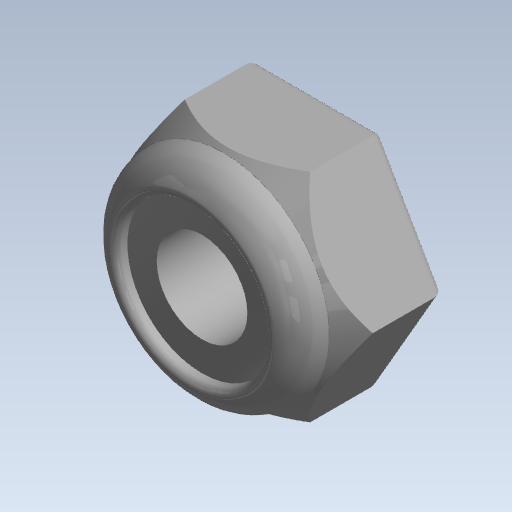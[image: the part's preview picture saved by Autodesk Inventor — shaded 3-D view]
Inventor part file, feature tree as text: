
AUTODESK INVENTOR PART (.ipt)
format: ipt  version: 2020 (Build 240168000, 168)  size: 135,680 bytes
history: native  units: mm (DEFAULTED — no unit token found)
features: fillet x1
ambient origin geometry x8: Origin, YZ Plane, XZ Plane, XY Plane, X Axis, Y Axis, Z Axis, Center Point
bodies: Solid1 (feature_tree)
feature tree (1):
  fillet  "Fillet5"  [1 undecoded]
note: 1 required parameter value undecoded (feature->parameter linkage not recoverable at this tier; creation-order binding heuristic only, values carry confidence <= 0.55)
